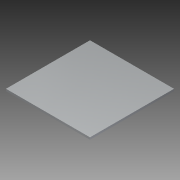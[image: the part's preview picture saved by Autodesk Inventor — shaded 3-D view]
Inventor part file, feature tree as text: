
AUTODESK INVENTOR PART (.ipt)
format: ipt  version: 2013 (Build 170138000, 138)  size: 68,096 bytes
history: native  units: mm
features: extrude x1, sketch x1
ambient origin geometry x8: Origin, YZ Plane, XZ Plane, XY Plane, X Axis, Y Axis, Z Axis, Center Point
bodies: Solid1 (feature_tree)
feature tree (2):
  extrude  "Extrusion1"  Depth=6.35mm TaperAngle=0.0deg
  sketch  "Sketch1"  dims[d0=254.0mm d1=6.35mm d2=0.0mm]
